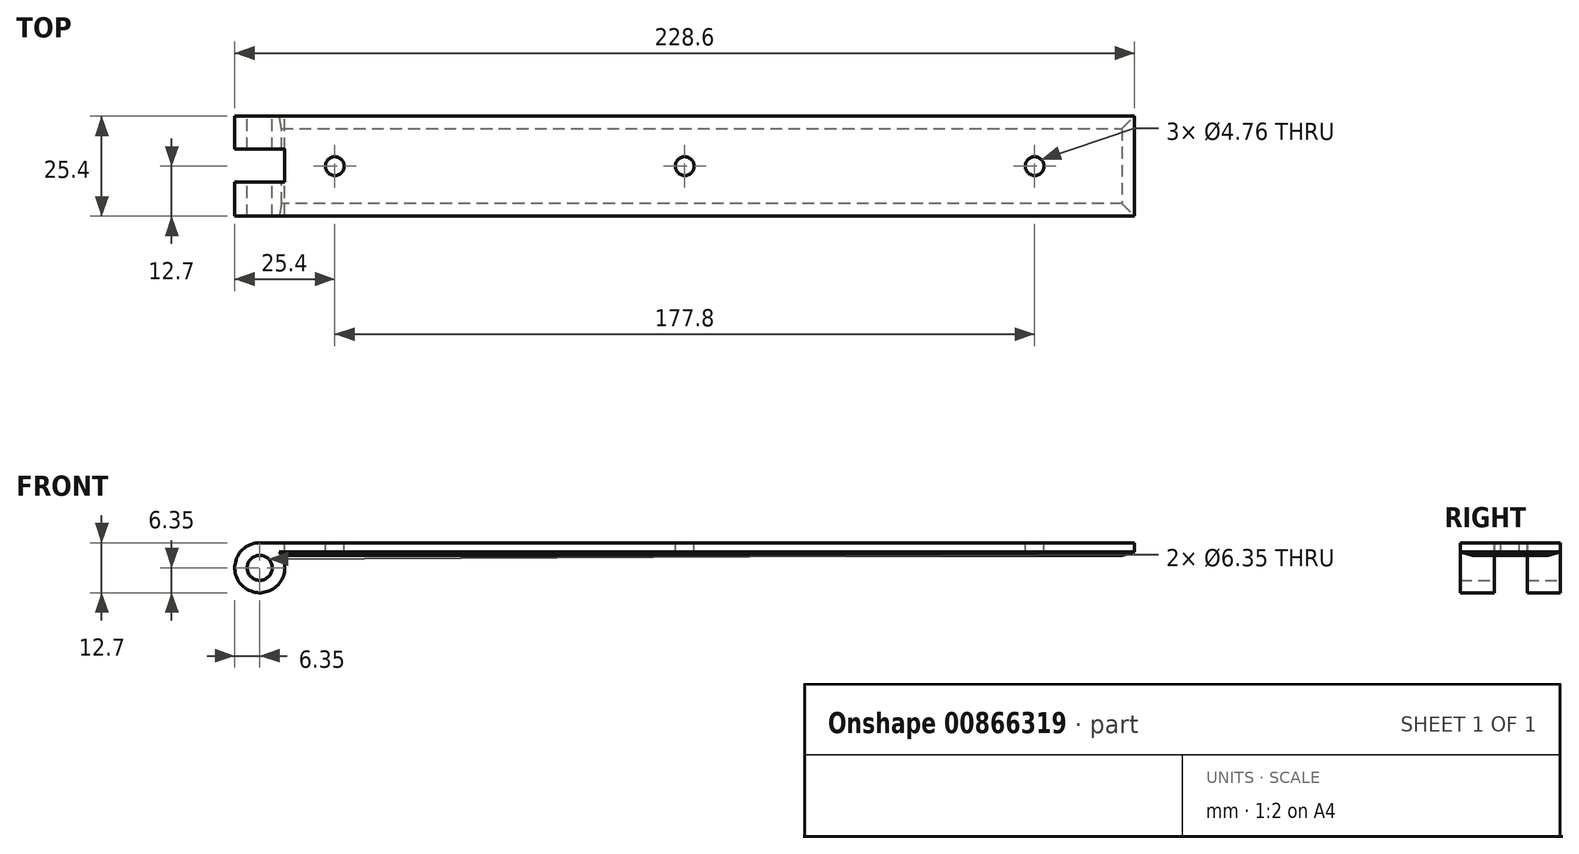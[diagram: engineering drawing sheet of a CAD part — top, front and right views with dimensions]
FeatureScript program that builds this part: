
annotation { "Feature Type Name" : "Feature", "Feature Type Description" : "" }
export const myFeature = defineFeature(function(context is Context, id is Id, definition is map)
    precondition{}
    {
        {
            var Q0;
            Q0=qCreatedBy(makeId("Front.planeOp"),FACE);
            var sketch = newSketch(context, id + "F0", { "sketchPlane" : qUnion([Q0])});
            skLineSegment(sketch, "E0.bottom", {"start": v(6.35, 0) * mm, "end": v(228.6, 0) * mm});
            skLineSegment(sketch, "E0.top", {"start": v(11.85, -3.18) * mm, "end": v(228.6, -3.18) * mm});
            skLineSegment(sketch, "E0.right", {"start": v(228.6, 0) * mm, "end": v(228.6, -3.17) * mm});
            skCircle(sketch, "E1", {"center": v(6.35, -6.35) * mm, "radius": 3.18 * mm});
            skArc(sketch, "E2.0", {"start": v(6.35, 0) * mm, "mid": v(3.17, -11.85) * mm, "end": v(11.85, -3.18) * mm});
            skSolve(sketch);
        }
        {
            var Q0;
            Q0=makeQuery(id+"F0.imprint","IMPRINT",FACE,{"disambiguationData":[TD([[makeQuery(id+"F0.imprint","IMPRINT",EDGE,{"derivedFrom":sQuery(id+"F0.wireOp",EDGE,"E0.bottom")}),-1.0]])]});
            extrude(context, id + "F1", {"entities" : qUnion([Q0]), "depth" : 25.4 * mm, "offsetDistance" : 25.4 * mm});
        }
        {
            var Q0;
            Q0=makeQuery(id+"F1.opExtrude","SWEPT_FACE",FACE,{"disambiguationData":[OSD([sQuery(id+"F0.wireOp",EDGE,"E0.bottom")])]});
            var sketch = newSketch(context, id + "F2", { "sketchPlane" : qUnion([Q0])});
            skCircle(sketch, "E3", {"center": v(203.2, -12.7) * mm, "radius": 2.38 * mm});
            skPoint(sketch, "E3.centerSnap0", {"position": v(228.6, -12.7) * mm});
            skCircle(sketch, "E4.1.0.0", {"center": v(114.3, -12.7) * mm, "radius": 2.38 * mm});
            skCircle(sketch, "E4.2.0.0", {"center": v(25.4, -12.7) * mm, "radius": 2.38 * mm});
            skLineSegment(sketch, "E4.direction1", {"start": v(203.2, -12.7) * mm, "end": v(114.3, -12.7) * mm, "construction": true});
            skSolve(sketch);
        }
        {
            var Q0;
            Q0 = qSketchRegion(id + "F2", true);
            extrude(context, id + "F3", {"entities" : qUnion([Q0]), "operationType" : NewBodyOperationType.REMOVE, "endBound" : BoundingType.UP_TO_NEXT, "oppositeDirection" : true, "depth" : 25.4 * mm, "offsetDistance" : 25.4 * mm});
        }
        {
            var Q0;
            Q0=makeQuery(id+"F1.opExtrude","SWEPT_FACE",FACE,{"disambiguationData":[OSD([sQuery(id+"F0.wireOp",EDGE,"E0.bottom")])]});
            var sketch = newSketch(context, id + "F4", { "sketchPlane" : qUnion([Q0])});
            skLineSegment(sketch, "E5.bottom", {"start": v(0, -8.38) * mm, "end": v(12.7, -8.38) * mm});
            skLineSegment(sketch, "E5.top", {"start": v(0, -16.76) * mm, "end": v(12.7, -16.76) * mm});
            skLineSegment(sketch, "E5.left", {"start": v(0, -8.38) * mm, "end": v(0, -16.76) * mm});
            skLineSegment(sketch, "E5.right", {"start": v(12.7, -8.38) * mm, "end": v(12.7, -16.76) * mm});
            skSolve(sketch);
        }
        {
            var Q0;
            Q0 = qSketchRegion(id + "F4", true);
            extrude(context, id + "F5", {"entities" : qUnion([Q0]), "operationType" : NewBodyOperationType.REMOVE, "endBound" : BoundingType.THROUGH_ALL, "oppositeDirection" : true, "depth" : 25.4 * mm, "offsetDistance" : 25.4 * mm});
        }
        {
            var Q0;
            Q0=makeQuery(id+"F1.opExtrude","CAP_EDGE",EDGE,{"disambiguationData":[OSD([sQuery(id+"F0.wireOp",EDGE,"E0.top")])],"isStart":false});
            var Q1;
            Q1=makeQuery(id+"F1.opExtrude","CAP_EDGE",EDGE,{"disambiguationData":[OSD([sQuery(id+"F0.wireOp",EDGE,"E0.top")])],"isStart":true});
            var Q2;
            Q2=makeQuery(id+"F1.opExtrude","SWEPT_EDGE",EDGE,{"disambiguationData":[OSD([sQuery(id+"F0.wireOp",EDGE,"E0.top"),sQuery(id+"F0.wireOp",EDGE,"E0.right")])]});
            chamfer(context, id + "F6", {"entities" : qUnion([Q0, Q1, Q2]), "chamferType" : ChamferType.TWO_OFFSETS, "width1" : 0.8 * mm, "oppositeDirection" : false, "width2" : 3.17 * mm, "tangentPropagation" : true});
        }
    });
